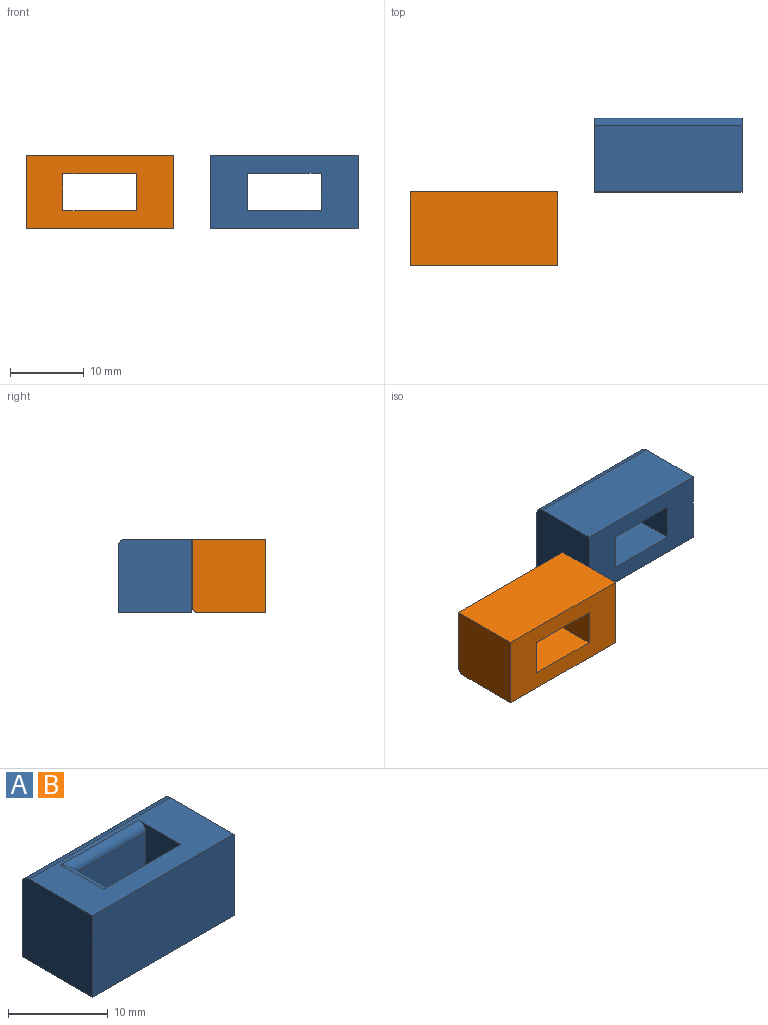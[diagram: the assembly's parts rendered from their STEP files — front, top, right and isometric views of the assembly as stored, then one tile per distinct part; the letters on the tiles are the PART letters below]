
ASSEMBLY  parts=2 mates=1
PART A: 13 faces, bbox 20x10x10 mm
  f0: plane 20x9mm, normal (0,0,1), area 114mm2, adj f3,f4,f5,f8,f9,f10,f11,f12
  f1: plane 20x10mm, normal (0,0,-1), area 150mm2, adj f2,f3,f4,f5,f6,f7,f8,f9
  f2: plane 20x9mm, normal (0,1,0), area 180mm2, adj f1,f3,f5,f10
  f3: plane 10x10mm, normal (-1,0,0), area 99.8mm2, adj f0,f1,f2,f4,f10
  f4: plane 20x10mm, normal (0,-1,0), area 200mm2, adj f0,f1,f3,f5
  f5: plane 10x10mm, normal (1,0,0), area 99.8mm2, adj f0,f1,f2,f4,f10
  f6: plane 10x9mm, normal (0,-1,0), area 90mm2, adj f1,f7,f9,f11
  f7: plane 9x5mm, normal (1,0,0), area 45mm2, adj f1,f6,f8,f12
  f8: plane 11x10mm, normal (0,1,0), area 100.2mm2, adj f0,f1,f7,f9,f12
  f9: plane 10x6mm, normal (-1,0,0), area 50.2mm2, adj f0,f1,f6,f8,f11
  f10: cylinder r=1mm len=20mm, axis (1,0,0), area 31.4mm2, adj f0,f2,f3,f5
  f11: cylinder r=1mm len=11mm, axis (1,0,0), area 16.3mm2, adj f0,f6,f9,f12
  f12: cylinder r=1mm len=6mm, axis (0,1,0), area 8.4mm2, adj f0,f7,f8,f11
PART B: same geometry as A
PLACE A rot(axis=(0,-0.71,-0.71),180deg) t=(40.76,16.52,2.21)mm
PLACE B rot(axis=(-1,0,0),90deg) t=(-4.24,6.52,-7.81)mm
MATE slider B.f3 <-> A.f5  axis (-1,0,0) through (-4.24,11.51,-2.8)mm
